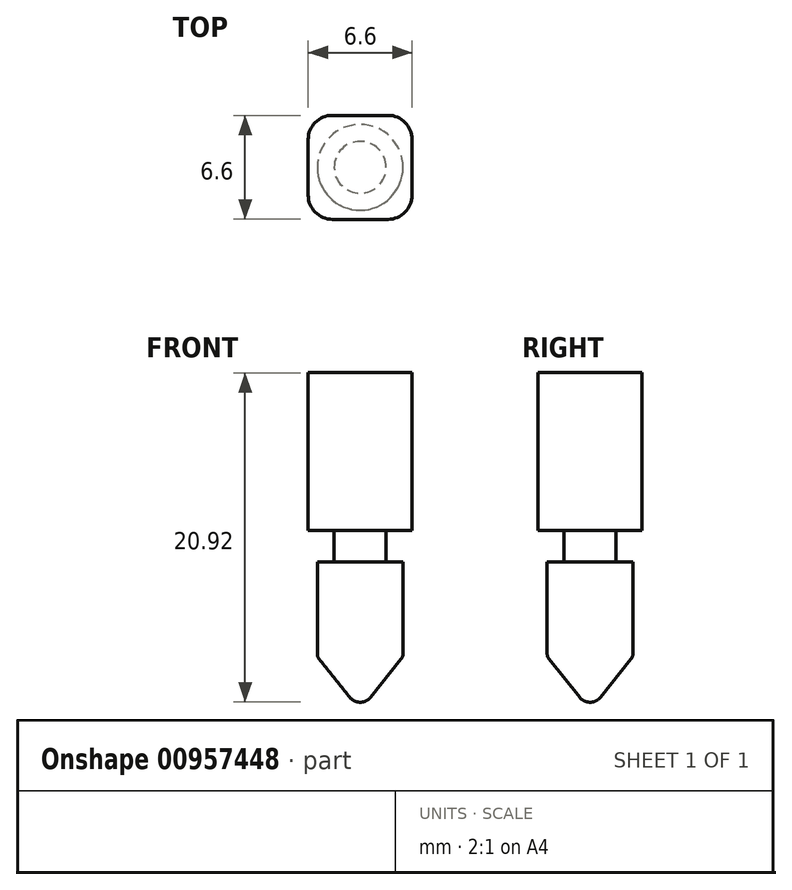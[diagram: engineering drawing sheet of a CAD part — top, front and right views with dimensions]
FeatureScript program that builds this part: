
annotation { "Feature Type Name" : "Feature", "Feature Type Description" : "" }
export const myFeature = defineFeature(function(context is Context, id is Id, definition is map)
    precondition{}
    {
        {
            var Q0;
            Q0=qCreatedBy(makeId("Top.planeOp"),FACE);
            var sketch = newSketch(context, id + "F0", { "sketchPlane" : qUnion([Q0])});
            skLineSegment(sketch, "E0.bottom", {"start": v(3.3, 3.3) * mm, "end": v(-3.3, 3.3) * mm});
            skLineSegment(sketch, "E0.top", {"start": v(3.3, -3.3) * mm, "end": v(-3.3, -3.3) * mm});
            skLineSegment(sketch, "E0.left", {"start": v(3.3, 3.3) * mm, "end": v(3.3, -3.3) * mm});
            skLineSegment(sketch, "E0.right", {"start": v(-3.3, 3.3) * mm, "end": v(-3.3, -3.3) * mm});
            skPoint(sketch, "E0.middle", {"position": v(0, 0) * mm});
            skSolve(sketch);
        }
        {
            var Q0;
            Q0=makeQuery(id+"F0.imprint","IMPRINT",FACE,{"disambiguationData":[TD([[makeQuery(id+"F0.imprint","IMPRINT",EDGE,{"derivedFrom":sQuery(id+"F0.wireOp",EDGE,"E0.bottom")}),1.0]])]});
            extrude(context, id + "F1", {"entities" : qUnion([Q0]), "depth" : 10.03 * mm, "offsetDistance" : 25.4 * mm});
        }
        {
            var Q0;
            Q0=makeQuery(id+"F1.opExtrude","CAP_FACE",FACE,{"disambiguationData":[OSD([sQuery(id+"F0.wireOp",EDGE,"E0.bottom"),sQuery(id+"F0.wireOp",EDGE,"E0.top"),sQuery(id+"F0.wireOp",EDGE,"E0.left"),sQuery(id+"F0.wireOp",EDGE,"E0.right")])],"isStart":true});
            var sketch = newSketch(context, id + "F2", { "sketchPlane" : qUnion([Q0])});
            skCircle(sketch, "E1", {"center": v(0, 0) * mm, "radius": 1.65 * mm});
            skSolve(sketch);
        }
        {
            var Q0;
            Q0=makeQuery(id+"F2.imprint","IMPRINT",FACE,{"disambiguationData":[TD([[makeQuery(id+"F2.imprint","IMPRINT",EDGE,{"derivedFrom":sQuery(id+"F2.wireOp",EDGE,"E1")}),1.0]])]});
            extrude(context, id + "F3", {"entities" : qUnion([Q0]), "operationType" : NewBodyOperationType.ADD, "depth" : 2.03 * mm, "offsetDistance" : 25.4 * mm});
        }
        {
            var Q0;
            Q0=makeQuery(id+"F1.opExtrude","SWEPT_FACE",FACE,{"disambiguationData":[OSD([sQuery(id+"F0.wireOp",EDGE,"E0.top")])]});
            var Q1;
            Q1=makeQuery(id+"F1.opExtrude","SWEPT_FACE",FACE,{"disambiguationData":[OSD([sQuery(id+"F0.wireOp",EDGE,"E0.bottom")])]});
            cPlane(context, id + "F4", {"entities" : qUnion([Q0, Q1]), "cplaneType" : CPlaneType.MID_PLANE, "offset" : 25.4 * mm, "width" : 152.4 * mm, "height" : 152.4 * mm});
        }
        {
            var Q0;
            Q0=qCreatedBy(id+"F4.planeOp",FACE);
            var sketch = newSketch(context, id + "F5", { "sketchPlane" : qUnion([Q0])});
            skLineSegment(sketch, "E2", {"start": v(1.61, -1.99) * mm, "end": v(2.72, -1.99) * mm});
            skLineSegment(sketch, "E3", {"start": v(2.72, -1.99) * mm, "end": v(2.72, -8) * mm});
            skLineSegment(sketch, "E4", {"start": v(2.72, -8) * mm, "end": v(0.4, -10.9) * mm});
            skLineSegment(sketch, "E5", {"start": v(0.4, -10.9) * mm, "end": v(0, -10.9) * mm});
            skLineSegment(sketch, "E6", {"start": v(0, -10.9) * mm, "end": v(0, -1.99) * mm});
            skLineSegment(sketch, "E7", {"start": v(0, -1.99) * mm, "end": v(1.61, -1.99) * mm});
            skSolve(sketch);
        }
        {
            var Q0;
            Q0=makeQuery(id+"F5.imprint","IMPRINT",FACE,{"disambiguationData":[TD([[makeQuery(id+"F5.imprint","IMPRINT",EDGE,{"derivedFrom":sQuery(id+"F5.wireOp",EDGE,"E2")}),-1.0]])]});
            var Q1;
            Q1=sQuery(id+"F5.wireOp",EDGE,"E6");
            revolve(context, id + "F6", {"operationType" : NewBodyOperationType.ADD, "surfaceOperationType" : NewSurfaceOperationType.NEW, "entities" : qUnion([Q0]), "axis" : qUnion([Q1]), "revolveType" : RevolveType.FULL});
        }
        {
            var Q0;
            Q0=makeQuery(id+"F6.opRevolve","SWEPT_EDGE",EDGE,{"disambiguationData":[OSD([sQuery(id+"F5.wireOp",EDGE,"E4"),sQuery(id+"F5.wireOp",EDGE,"E5")])]});
            fillet(context, id + "F7", {"entities" : qUnion([Q0]), "radius" : 0.81 * mm, "tangentPropagation" : true, "allowEdgeOverflow" : false});
        }
        {
            var Q0;
            Q0=makeQuery(id+"F1.opExtrude","SWEPT_EDGE",EDGE,{"disambiguationData":[OSD([sQuery(id+"F0.wireOp",EDGE,"E0.top"),sQuery(id+"F0.wireOp",EDGE,"E0.right")])]});
            var Q1;
            Q1=makeQuery(id+"F1.opExtrude","SWEPT_EDGE",EDGE,{"disambiguationData":[OSD([sQuery(id+"F0.wireOp",EDGE,"E0.top"),sQuery(id+"F0.wireOp",EDGE,"E0.left")])]});
            var Q2;
            Q2=makeQuery(id+"F1.opExtrude","SWEPT_EDGE",EDGE,{"disambiguationData":[OSD([sQuery(id+"F0.wireOp",EDGE,"E0.bottom"),sQuery(id+"F0.wireOp",EDGE,"E0.left")])]});
            var Q3;
            Q3=makeQuery(id+"F1.opExtrude","SWEPT_EDGE",EDGE,{"disambiguationData":[OSD([sQuery(id+"F0.wireOp",EDGE,"E0.bottom"),sQuery(id+"F0.wireOp",EDGE,"E0.right")])]});
            fillet(context, id + "F8", {"entities" : qUnion([Q0, Q1, Q2, Q3]), "radius" : 1.53 * mm, "tangentPropagation" : true, "allowEdgeOverflow" : false});
        }
        {
            var Q0;
            Q0=makeQuery(id+"F6.opRevolve","SWEPT_EDGE",EDGE,{"disambiguationData":[OSD([sQuery(id+"F5.wireOp",EDGE,"E3"),sQuery(id+"F5.wireOp",EDGE,"E4")])]});
            fillet(context, id + "F9", {"entities" : qUnion([Q0]), "radius" : 0.55 * mm, "tangentPropagation" : true, "allowEdgeOverflow" : false});
        }
    });
